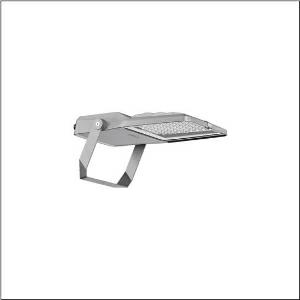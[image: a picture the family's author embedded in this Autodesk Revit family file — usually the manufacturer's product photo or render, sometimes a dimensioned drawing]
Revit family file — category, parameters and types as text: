
# Revit family: floodlight_fl_21_mini___pl52_5xa7775c2d1a_7e4d
name_source: partatom
category: Lighting Fixtures
units: mm (PartAtom-declared; Revit-internal decimal feet)

## family parameters
Cut with Voids When Loaded = No
Host = Face
Light Source = No
Part Type = Normal
Room Calculation Point = No
Round Connector Dimension = Use Diameter
Shared = No

## types (1)
- --- (1 x LED, 12190 lm, 89 W, 3000K)
    Apparent Load = 89 VA
    CIE Flux Codes = 26 60 98 100 100
    Color Rendering = 70
    Color Temperature = 3000K
    Default Elevation = 1800 mm
    Description = Floodlight FL 21 mini, floodlight, primary light control with lens, of PMMA, primary optical cover: protective disc, of toughened safety glass, transparent, light distribution: PL52, light emission: direct distribution, installation type: surface-mounted, LED, High Power LED, rated luminous flux: 12.190lm, luminous efficacy: 137lm/W, light colour: 730, colour temperature: 3000K, control gear: Smart Interface (Zhaga), control: flexible luminous flux parameterisation, time-dependent luminous flux control, constant luminous flux control, overheat protection, pre-setting: logarithmic dimming characteristic, with terminal, 6-pole, mains connection: 220..240V, AC, 50/60Hz, start of lifetime: 89W, end of service life: 94W, reduction: 43W, luminaire housing, of diecast aluminium, powder-coated, Siteco® metallic grey (DB 702S), corrosivity category C5 mid according to DIN EN ISO 12944, suitable for swimming pools, chlorine-resistant, sealing non-destructively replaceable, mounting bracket, of steel, galvanised, powder-coated, Siteco® metallic grey (DB 702S), Smart Interface above, protection rating (complete): IP66, insulation class (complete): insulation class II (safety insulation), certification: CE, ENEC, VDE, protection symbol: D, impact resistance: IK08, permissible operating ambient temperature: -40..+40°C, permissible operating ambient temperature for outdoor applications: -40..+50°C, standard: DIN EN 12944, LABS conformity tested according to VDMA 24364:2018-05, packaging unit: 1 piece

Light Distribution: PL52
    Height = 70 mm
    Lamp = 1 x LED
    Lamp Light Flux = 12190 lm
    Lamp Power = 89 W
    Lamp count = 1
    Length = 485 mm
    Luminous efficacy = 137 lm/W
    Manufacturer = Siteco
    ModVariant = No
    Model = 5XA7775C2D1A
    Number of Poles = 1
    OnlyDefault = Yes
    Power Factor = 1
    Product Name = Floodlight FL 21 mini | PL52
    Product group = floodlight | pylon annexe
    ProductGroupID = 6200
    Protection Class = Protection class II
    Protection Degree = IP 66
    RLX_Detail_Level = 1
    RLX_Emergency_Light_Flux = 0 lm
    RLX_Emergency_Type = 0
    RLX_Emergency_Type_DB = No
    RlxData = <blob elided: 96085 chars, md5=26bd7587>
    Socket = socket
    Standby Power = 0 W
    System Light Flux = 12190 lm
    System Power = 89 W
    Type Comments = factory setting: luminous flux: 100 % | dim-lin: 254 | 456 mA
    Type Image = l_1006845.jpg
    URL = http://relux.com
    VarID = @adj_163354
    Voltage = 0 V
    Weight = 0.00 kg
    Width = 337 mm

## geometry (parser evidence)
native form markers: Blend x4, Sweep x14
no freeform markers — native parametric forms only
